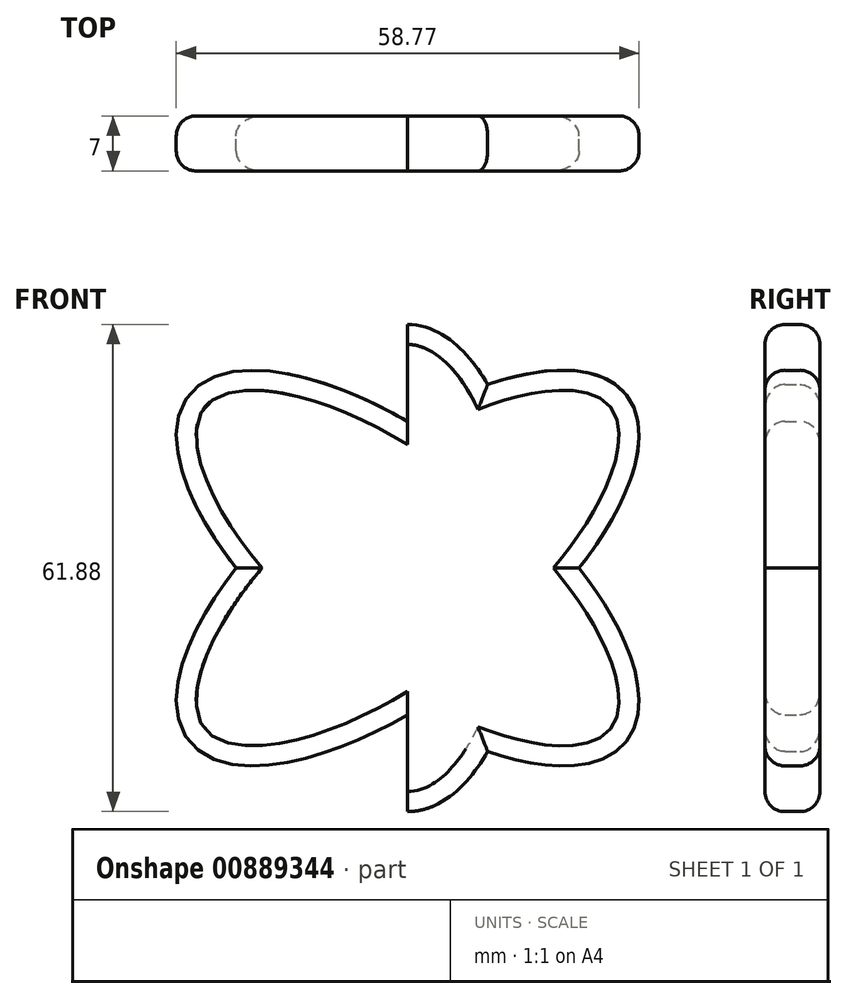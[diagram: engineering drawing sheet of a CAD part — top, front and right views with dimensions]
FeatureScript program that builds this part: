
annotation { "Feature Type Name" : "Feature", "Feature Type Description" : "" }
export const myFeature = defineFeature(function(context is Context, id is Id, definition is map)
    precondition{}
    {
        {
            var Q0;
            Q0=qCreatedBy(makeId("Front.planeOp"),FACE);
            var sketch = newSketch(context, id + "F0", { "sketchPlane" : qUnion([Q0])});
            skEllipse(sketch, "E0", {"center": v(0, 0) * mm, "majorRadius": 30.94 * mm, "minorRadius": 15.45 * mm, "majorAxis": v(0, -1)});
            skEllipse(sketch, "E1", {"center": v(0, 0) * mm, "majorRadius": 35.44 * mm, "minorRadius": 15.45 * mm, "majorAxis": v(0.78, -0.62)});
            skEllipse(sketch, "E2.MirrorC", {"center": v(0, 0) * mm, "majorRadius": 35.44 * mm, "minorRadius": 15.45 * mm, "majorAxis": v(-0.78, -0.62)});
            skLineSegment(sketch, "E3", {"start": v(0, 30.94) * mm, "end": v(0, -30.94) * mm});
            skSolve(sketch);
        }
        {
            var Q0;
            {var subQ0=sQuery(id+"F0.wireOp",EDGE,"E2.MirrorC");var subQ1=sQuery(id+"F0.wireOp",EDGE,"E0");var subQ2=makeQuery(id+"F0.imprint","INTERSECT",VERTEX,{"disambiguationData":[OD(0.0)],"derivedFrom":[subQ1,subQ0]});Q0=makeQuery(id+"F0.imprint","IMPRINT",FACE,{"disambiguationData":[TD([[makeQuery(id+"F0.imprint","IMPRINT",EDGE,{"disambiguationData":[TD([[subQ2,-1.0]])],"derivedFrom":subQ1}),1.0]])]});}
            var Q1;
            {var subQ0=sQuery(id+"F0.wireOp",EDGE,"E1");var subQ1=sQuery(id+"F0.wireOp",EDGE,"E0");var subQ2=makeQuery(id+"F0.imprint","INTERSECT",VERTEX,{"disambiguationData":[OD(1.0)],"derivedFrom":[subQ1,subQ0]});Q1=makeQuery(id+"F0.imprint","IMPRINT",FACE,{"disambiguationData":[TD([[makeQuery(id+"F0.imprint","IMPRINT",EDGE,{"disambiguationData":[TD([[subQ2,-1.0]])],"derivedFrom":subQ1}),-1.0]])]});}
            var Q2;
            {var subQ0=sQuery(id+"F0.wireOp",EDGE,"E2.MirrorC");var subQ1=sQuery(id+"F0.wireOp",EDGE,"E0");var subQ2=makeQuery(id+"F0.imprint","INTERSECT",VERTEX,{"disambiguationData":[OD(0.0)],"derivedFrom":[subQ1,subQ0]});Q2=makeQuery(id+"F0.imprint","IMPRINT",FACE,{"disambiguationData":[TD([[makeQuery(id+"F0.imprint","IMPRINT",EDGE,{"disambiguationData":[TD([[subQ2,1.0]])],"derivedFrom":subQ1}),-1.0]])]});}
            var Q3;
            {var subQ0=sQuery(id+"F0.wireOp",EDGE,"E1");var subQ1=sQuery(id+"F0.wireOp",EDGE,"E0");var subQ2=makeQuery(id+"F0.imprint","INTERSECT",VERTEX,{"disambiguationData":[OD(0.0)],"derivedFrom":[subQ1,subQ0]});Q3=makeQuery(id+"F0.imprint","IMPRINT",FACE,{"disambiguationData":[TD([[makeQuery(id+"F0.imprint","IMPRINT",EDGE,{"disambiguationData":[TD([[subQ2,-1.0]])],"derivedFrom":subQ1}),-1.0]])]});}
            var Q4;
            {var subQ0=sQuery(id+"F0.wireOp",EDGE,"E2.MirrorC");var subQ1=sQuery(id+"F0.wireOp",EDGE,"E0");var subQ2=makeQuery(id+"F0.imprint","INTERSECT",VERTEX,{"disambiguationData":[OD(1.0)],"derivedFrom":[subQ1,subQ0]});Q4=makeQuery(id+"F0.imprint","IMPRINT",FACE,{"disambiguationData":[TD([[makeQuery(id+"F0.imprint","IMPRINT",EDGE,{"disambiguationData":[TD([[subQ2,1.0]])],"derivedFrom":subQ1}),-1.0]])]});}
            var Q5;
            {var subQ0=sQuery(id+"F0.wireOp",EDGE,"E1");var subQ1=sQuery(id+"F0.wireOp",EDGE,"E0");var subQ2=makeQuery(id+"F0.imprint","INTERSECT",VERTEX,{"disambiguationData":[OD(0.0)],"derivedFrom":[subQ1,subQ0]});Q5=makeQuery(id+"F0.imprint","IMPRINT",FACE,{"disambiguationData":[TD([[makeQuery(id+"F0.imprint","IMPRINT",EDGE,{"disambiguationData":[TD([[subQ2,1.0]])],"derivedFrom":subQ1}),1.0]])]});}
            var Q6;
            Q6=makeQuery(id+"F0.imprint","IMPRINT",FACE,{"disambiguationData":[TD([[makeQuery(id+"F0.imprint","IMPRINT",EDGE,{"derivedFrom":sQuery(id+"F0.wireOp",EDGE,"LZZV73RN-npso-72dP-JXCp-cFYvsp7JB5Xd")}),-1.0]])]});
            var Q7;
            {var subQ0=sQuery(id+"F0.wireOp",EDGE,"Dlmi2PQk-qXYu-TZ0k-GXdR-v94EXzE1gpfV");var subQ1=sQuery(id+"F0.wireOp",EDGE,"E2.MirrorC");var subQ2=makeQuery(id+"F0.imprint","INTERSECT",VERTEX,{"disambiguationData":[OD(2.0)],"derivedFrom":[subQ1,subQ0]});Q7=makeQuery(id+"F0.imprint","IMPRINT",FACE,{"disambiguationData":[TD([[makeQuery(id+"F0.imprint","IMPRINT",EDGE,{"disambiguationData":[TD([[subQ2,-1.0]])],"derivedFrom":subQ1}),1.0]])]});}
            var Q8;
            {var subQ0=sQuery(id+"F0.wireOp",EDGE,"Dlmi2PQk-qXYu-TZ0k-GXdR-v94EXzE1gpfV");var subQ1=sQuery(id+"F0.wireOp",EDGE,"E2.MirrorC");var subQ2=makeQuery(id+"F0.imprint","INTERSECT",VERTEX,{"disambiguationData":[OD(0.0)],"derivedFrom":[subQ1,subQ0]});Q8=makeQuery(id+"F0.imprint","IMPRINT",FACE,{"disambiguationData":[TD([[makeQuery(id+"F0.imprint","IMPRINT",EDGE,{"disambiguationData":[TD([[subQ2,-1.0]])],"derivedFrom":subQ1}),1.0]])]});}
            var Q9;
            {var subQ0=sQuery(id+"F0.wireOp",EDGE,"hAAybYIK-r48V-uU67-k7O7-xJTClFqp8aIw");var subQ1=sQuery(id+"F0.wireOp",EDGE,"E1");var subQ2=makeQuery(id+"F0.imprint","INTERSECT",VERTEX,{"disambiguationData":[OD(1.0)],"derivedFrom":[subQ1,subQ0]});Q9=makeQuery(id+"F0.imprint","IMPRINT",FACE,{"disambiguationData":[TD([[makeQuery(id+"F0.imprint","IMPRINT",EDGE,{"disambiguationData":[TD([[subQ2,-1.0]])],"derivedFrom":subQ1}),1.0]])]});}
            var Q10;
            {var subQ0=sQuery(id+"F0.wireOp",EDGE,"hAAybYIK-r48V-uU67-k7O7-xJTClFqp8aIw");var subQ1=sQuery(id+"F0.wireOp",EDGE,"E1");var subQ2=makeQuery(id+"F0.imprint","INTERSECT",VERTEX,{"disambiguationData":[OD(1.0)],"derivedFrom":[subQ1,subQ0]});Q10=makeQuery(id+"F0.imprint","IMPRINT",FACE,{"disambiguationData":[TD([[makeQuery(id+"F0.imprint","IMPRINT",EDGE,{"disambiguationData":[TD([[subQ2,-1.0]])],"derivedFrom":subQ1}),-1.0]])]});}
            var Q11;
            {var subQ0=sQuery(id+"F0.wireOp",EDGE,"E1");var subQ1=sQuery(id+"F0.wireOp",EDGE,"E0");var subQ2=makeQuery(id+"F0.imprint","INTERSECT",VERTEX,{"disambiguationData":[OD(2.0)],"derivedFrom":[subQ1,subQ0]});Q11=makeQuery(id+"F0.imprint","IMPRINT",FACE,{"disambiguationData":[TD([[makeQuery(id+"F0.imprint","IMPRINT",EDGE,{"disambiguationData":[TD([[subQ2,-1.0]])],"derivedFrom":subQ1}),1.0]])]});}
            var Q12;
            {var subQ0=sQuery(id+"F0.wireOp",EDGE,"E2.MirrorC");var subQ1=sQuery(id+"F0.wireOp",EDGE,"E0");var subQ2=makeQuery(id+"F0.imprint","INTERSECT",VERTEX,{"disambiguationData":[OD(0.0)],"derivedFrom":[subQ1,subQ0]});Q12=makeQuery(id+"F0.imprint","IMPRINT",FACE,{"disambiguationData":[TD([[makeQuery(id+"F0.imprint","IMPRINT",EDGE,{"disambiguationData":[TD([[subQ2,1.0]])],"derivedFrom":subQ1}),1.0]])]});}
            var Q13;
            {var subQ0=sQuery(id+"F0.wireOp",EDGE,"hAAybYIK-r48V-uU67-k7O7-xJTClFqp8aIw");var subQ1=sQuery(id+"F0.wireOp",EDGE,"E0");var subQ2=makeQuery(id+"F0.imprint","INTERSECT",VERTEX,{"disambiguationData":[OD(0.0)],"derivedFrom":[subQ1,subQ0]});Q13=makeQuery(id+"F0.imprint","IMPRINT",FACE,{"disambiguationData":[TD([[makeQuery(id+"F0.imprint","IMPRINT",EDGE,{"disambiguationData":[TD([[subQ2,-1.0]])],"derivedFrom":subQ1}),1.0]])]});}
            var Q14;
            {var subQ0=sQuery(id+"F0.wireOp",EDGE,"Dlmi2PQk-qXYu-TZ0k-GXdR-v94EXzE1gpfV");var subQ1=sQuery(id+"F0.wireOp",EDGE,"E0");var subQ2=makeQuery(id+"F0.imprint","INTERSECT",VERTEX,{"disambiguationData":[OD(1.0)],"derivedFrom":[subQ1,subQ0]});Q14=makeQuery(id+"F0.imprint","IMPRINT",FACE,{"disambiguationData":[TD([[makeQuery(id+"F0.imprint","IMPRINT",EDGE,{"disambiguationData":[TD([[subQ2,-1.0]])],"derivedFrom":subQ1}),1.0]])]});}
            var Q15;
            {var subQ0=sQuery(id+"F0.wireOp",EDGE,"Dlmi2PQk-qXYu-TZ0k-GXdR-v94EXzE1gpfV");var subQ1=sQuery(id+"F0.wireOp",EDGE,"E0");var subQ2=makeQuery(id+"F0.imprint","INTERSECT",VERTEX,{"disambiguationData":[OD(1.0)],"derivedFrom":[subQ1,subQ0]});Q15=makeQuery(id+"F0.imprint","IMPRINT",FACE,{"disambiguationData":[TD([[makeQuery(id+"F0.imprint","IMPRINT",EDGE,{"disambiguationData":[TD([[subQ2,-1.0]])],"derivedFrom":subQ1}),-1.0]])]});}
            var Q16;
            {var subQ0=sQuery(id+"F0.wireOp",EDGE,"E2.MirrorC");var subQ1=sQuery(id+"F0.wireOp",EDGE,"E0");var subQ2=makeQuery(id+"F0.imprint","INTERSECT",VERTEX,{"disambiguationData":[OD(2.0)],"derivedFrom":[subQ1,subQ0]});Q16=makeQuery(id+"F0.imprint","IMPRINT",FACE,{"disambiguationData":[TD([[makeQuery(id+"F0.imprint","IMPRINT",EDGE,{"disambiguationData":[TD([[subQ2,-1.0]])],"derivedFrom":subQ1}),-1.0]])]});}
            var Q17;
            {var subQ0=sQuery(id+"F0.wireOp",EDGE,"E2.MirrorC");var subQ1=sQuery(id+"F0.wireOp",EDGE,"E1");var subQ2=makeQuery(id+"F0.imprint","INTERSECT",VERTEX,{"disambiguationData":[OD(0.0)],"derivedFrom":[subQ1,subQ0]});Q17=makeQuery(id+"F0.imprint","IMPRINT",FACE,{"disambiguationData":[TD([[makeQuery(id+"F0.imprint","IMPRINT",EDGE,{"disambiguationData":[TD([[subQ2,-1.0]])],"derivedFrom":subQ1}),1.0]])]});}
            var Q18;
            {var subQ0=sQuery(id+"F0.wireOp",EDGE,"Dlmi2PQk-qXYu-TZ0k-GXdR-v94EXzE1gpfV");var subQ1=sQuery(id+"F0.wireOp",EDGE,"E0");var subQ2=makeQuery(id+"F0.imprint","INTERSECT",VERTEX,{"disambiguationData":[OD(2.0)],"derivedFrom":[subQ1,subQ0]});Q18=makeQuery(id+"F0.imprint","IMPRINT",FACE,{"disambiguationData":[TD([[makeQuery(id+"F0.imprint","IMPRINT",EDGE,{"disambiguationData":[TD([[subQ2,-1.0]])],"derivedFrom":subQ1}),1.0]])]});}
            var Q19;
            {var subQ0=sQuery(id+"F0.wireOp",EDGE,"E1");var subQ1=sQuery(id+"F0.wireOp",EDGE,"E0");var subQ2=makeQuery(id+"F0.imprint","INTERSECT",VERTEX,{"disambiguationData":[OD(1.0)],"derivedFrom":[subQ1,subQ0]});Q19=makeQuery(id+"F0.imprint","IMPRINT",FACE,{"disambiguationData":[TD([[makeQuery(id+"F0.imprint","IMPRINT",EDGE,{"disambiguationData":[TD([[subQ2,-1.0]])],"derivedFrom":subQ1}),1.0]])]});}
            var Q20;
            {var subQ0=sQuery(id+"F0.wireOp",EDGE,"E2.MirrorC");var subQ1=sQuery(id+"F0.wireOp",EDGE,"E1");var subQ2=makeQuery(id+"F0.imprint","INTERSECT",VERTEX,{"disambiguationData":[OD(2.0)],"derivedFrom":[subQ1,subQ0]});Q20=makeQuery(id+"F0.imprint","IMPRINT",FACE,{"disambiguationData":[TD([[makeQuery(id+"F0.imprint","IMPRINT",EDGE,{"disambiguationData":[TD([[subQ2,-1.0]])],"derivedFrom":subQ1}),1.0]])]});}
            var Q21;
            {var subQ0=sQuery(id+"F0.wireOp",EDGE,"E2.MirrorC");var subQ1=sQuery(id+"F0.wireOp",EDGE,"E0");var subQ2=makeQuery(id+"F0.imprint","INTERSECT",VERTEX,{"disambiguationData":[OD(3.0)],"derivedFrom":[subQ1,subQ0]});Q21=makeQuery(id+"F0.imprint","IMPRINT",FACE,{"disambiguationData":[TD([[makeQuery(id+"F0.imprint","IMPRINT",EDGE,{"disambiguationData":[TD([[subQ2,-1.0]])],"derivedFrom":subQ1}),-1.0]])]});}
            var Q22;
            {var subQ0=sQuery(id+"F0.wireOp",EDGE,"E2.MirrorC");var subQ1=sQuery(id+"F0.wireOp",EDGE,"E0");var subQ2=makeQuery(id+"F0.imprint","INTERSECT",VERTEX,{"disambiguationData":[OD(3.0)],"derivedFrom":[subQ1,subQ0]});Q22=makeQuery(id+"F0.imprint","IMPRINT",FACE,{"disambiguationData":[TD([[makeQuery(id+"F0.imprint","IMPRINT",EDGE,{"disambiguationData":[TD([[subQ2,-1.0]])],"derivedFrom":subQ1}),1.0]])]});}
            var Q23;
            {var subQ0=sQuery(id+"F0.wireOp",EDGE,"Dlmi2PQk-qXYu-TZ0k-GXdR-v94EXzE1gpfV");var subQ1=sQuery(id+"F0.wireOp",EDGE,"E0");var subQ2=makeQuery(id+"F0.imprint","INTERSECT",VERTEX,{"disambiguationData":[OD(3.0)],"derivedFrom":[subQ1,subQ0]});Q23=makeQuery(id+"F0.imprint","IMPRINT",FACE,{"disambiguationData":[TD([[makeQuery(id+"F0.imprint","IMPRINT",EDGE,{"disambiguationData":[TD([[subQ2,-1.0]])],"derivedFrom":subQ1}),-1.0]])]});}
            var Q24;
            {var subQ0=sQuery(id+"F0.wireOp",EDGE,"Dlmi2PQk-qXYu-TZ0k-GXdR-v94EXzE1gpfV");var subQ1=sQuery(id+"F0.wireOp",EDGE,"E0");var subQ2=makeQuery(id+"F0.imprint","INTERSECT",VERTEX,{"disambiguationData":[OD(3.0)],"derivedFrom":[subQ1,subQ0]});Q24=makeQuery(id+"F0.imprint","IMPRINT",FACE,{"disambiguationData":[TD([[makeQuery(id+"F0.imprint","IMPRINT",EDGE,{"disambiguationData":[TD([[subQ2,-1.0]])],"derivedFrom":subQ1}),1.0]])]});}
            var Q25;
            {var subQ0=sQuery(id+"F0.wireOp",EDGE,"E1");var subQ1=sQuery(id+"F0.wireOp",EDGE,"E0");var subQ2=makeQuery(id+"F0.imprint","INTERSECT",VERTEX,{"disambiguationData":[OD(3.0)],"derivedFrom":[subQ1,subQ0]});Q25=makeQuery(id+"F0.imprint","IMPRINT",FACE,{"disambiguationData":[TD([[makeQuery(id+"F0.imprint","IMPRINT",EDGE,{"disambiguationData":[TD([[subQ2,-1.0]])],"derivedFrom":subQ1}),1.0]])]});}
            var Q26;
            {var subQ0=sQuery(id+"F0.wireOp",EDGE,"E2.MirrorC");var subQ1=sQuery(id+"F0.wireOp",EDGE,"E0");var subQ2=makeQuery(id+"F0.imprint","INTERSECT",VERTEX,{"disambiguationData":[OD(1.0)],"derivedFrom":[subQ1,subQ0]});Q26=makeQuery(id+"F0.imprint","IMPRINT",FACE,{"disambiguationData":[TD([[makeQuery(id+"F0.imprint","IMPRINT",EDGE,{"disambiguationData":[TD([[subQ2,1.0]])],"derivedFrom":subQ1}),1.0]])]});}
            var Q27;
            {var subQ0=sQuery(id+"F0.wireOp",EDGE,"hAAybYIK-r48V-uU67-k7O7-xJTClFqp8aIw");var subQ1=sQuery(id+"F0.wireOp",EDGE,"E1");var subQ2=makeQuery(id+"F0.imprint","INTERSECT",VERTEX,{"disambiguationData":[OD(3.0)],"derivedFrom":[subQ1,subQ0]});Q27=makeQuery(id+"F0.imprint","IMPRINT",FACE,{"disambiguationData":[TD([[makeQuery(id+"F0.imprint","IMPRINT",EDGE,{"disambiguationData":[TD([[subQ2,-1.0]])],"derivedFrom":subQ1}),-1.0]])]});}
            var Q28;
            {var subQ0=sQuery(id+"F0.wireOp",EDGE,"E2.MirrorC");var subQ1=sQuery(id+"F0.wireOp",EDGE,"E1");var subQ2=makeQuery(id+"F0.imprint","INTERSECT",VERTEX,{"disambiguationData":[OD(1.0)],"derivedFrom":[subQ1,subQ0]});Q28=makeQuery(id+"F0.imprint","IMPRINT",FACE,{"disambiguationData":[TD([[makeQuery(id+"F0.imprint","IMPRINT",EDGE,{"disambiguationData":[TD([[subQ2,-1.0]])],"derivedFrom":subQ1}),1.0]])]});}
            var Q29;
            {var subQ0=sQuery(id+"F0.wireOp",EDGE,"Dlmi2PQk-qXYu-TZ0k-GXdR-v94EXzE1gpfV");var subQ1=sQuery(id+"F0.wireOp",EDGE,"E0");var subQ2=makeQuery(id+"F0.imprint","INTERSECT",VERTEX,{"disambiguationData":[OD(0.0)],"derivedFrom":[subQ1,subQ0]});Q29=makeQuery(id+"F0.imprint","IMPRINT",FACE,{"disambiguationData":[TD([[makeQuery(id+"F0.imprint","IMPRINT",EDGE,{"disambiguationData":[TD([[subQ2,-1.0]])],"derivedFrom":subQ1}),1.0]])]});}
            var Q30;
            {var subQ0=sQuery(id+"F0.wireOp",EDGE,"E2.MirrorC");var subQ1=sQuery(id+"F0.wireOp",EDGE,"E0");var subQ2=makeQuery(id+"F0.imprint","INTERSECT",VERTEX,{"disambiguationData":[OD(2.0)],"derivedFrom":[subQ1,subQ0]});Q30=makeQuery(id+"F0.imprint","IMPRINT",FACE,{"disambiguationData":[TD([[makeQuery(id+"F0.imprint","IMPRINT",EDGE,{"disambiguationData":[TD([[subQ2,-1.0]])],"derivedFrom":subQ1}),1.0]])]});}
            var Q31;
            {var subQ0=sQuery(id+"F0.wireOp",EDGE,"E1");var subQ1=sQuery(id+"F0.wireOp",EDGE,"E0");var subQ2=makeQuery(id+"F0.imprint","INTERSECT",VERTEX,{"disambiguationData":[OD(0.0)],"derivedFrom":[subQ1,subQ0]});Q31=makeQuery(id+"F0.imprint","IMPRINT",FACE,{"disambiguationData":[TD([[makeQuery(id+"F0.imprint","IMPRINT",EDGE,{"disambiguationData":[TD([[subQ2,-1.0]])],"derivedFrom":subQ1}),1.0]])]});}
            var Q32;
            {var subQ0=sQuery(id+"F0.wireOp",EDGE,"E2.MirrorC");var subQ1=sQuery(id+"F0.wireOp",EDGE,"E1");var subQ2=makeQuery(id+"F0.imprint","INTERSECT",VERTEX,{"disambiguationData":[OD(3.0)],"derivedFrom":[subQ1,subQ0]});Q32=makeQuery(id+"F0.imprint","IMPRINT",FACE,{"disambiguationData":[TD([[makeQuery(id+"F0.imprint","IMPRINT",EDGE,{"disambiguationData":[TD([[subQ2,-1.0]])],"derivedFrom":subQ1}),1.0]])]});}
            var Q33;
            {var subQ0=sQuery(id+"F0.wireOp",EDGE,"hAAybYIK-r48V-uU67-k7O7-xJTClFqp8aIw");var subQ1=sQuery(id+"F0.wireOp",EDGE,"E0");var subQ2=makeQuery(id+"F0.imprint","INTERSECT",VERTEX,{"disambiguationData":[OD(2.0)],"derivedFrom":[subQ1,subQ0]});Q33=makeQuery(id+"F0.imprint","IMPRINT",FACE,{"disambiguationData":[TD([[makeQuery(id+"F0.imprint","IMPRINT",EDGE,{"disambiguationData":[TD([[subQ2,-1.0]])],"derivedFrom":subQ1}),1.0]])]});}
            var Q34;
            {var subQ0=sQuery(id+"F0.wireOp",EDGE,"rtznIF7v-u61m-MHR9-NeHj-gsrXDnTg4Oiu");var subQ1=sQuery(id+"F0.wireOp",EDGE,"E1");var subQ2=makeQuery(id+"F0.imprint","INTERSECT",VERTEX,{"disambiguationData":[OD(2.0)],"derivedFrom":[subQ1,subQ0]});Q34=makeQuery(id+"F0.imprint","IMPRINT",FACE,{"disambiguationData":[TD([[makeQuery(id+"F0.imprint","IMPRINT",EDGE,{"disambiguationData":[TD([[subQ2,-1.0]])],"derivedFrom":subQ1}),1.0]])]});}
            var Q35;
            {var subQ0=sQuery(id+"F0.wireOp",EDGE,"hAAybYIK-r48V-uU67-k7O7-xJTClFqp8aIw");var subQ1=sQuery(id+"F0.wireOp",EDGE,"E1");var subQ2=makeQuery(id+"F0.imprint","INTERSECT",VERTEX,{"disambiguationData":[OD(3.0)],"derivedFrom":[subQ1,subQ0]});Q35=makeQuery(id+"F0.imprint","IMPRINT",FACE,{"disambiguationData":[TD([[makeQuery(id+"F0.imprint","IMPRINT",EDGE,{"disambiguationData":[TD([[subQ2,-1.0]])],"derivedFrom":subQ1}),1.0]])]});}
            extrude(context, id + "F1", {"entities" : qUnion([Q0, Q1, Q2, Q3, Q4, Q5, Q6, Q7, Q8, Q9, Q10, Q11, Q12, Q13, Q14, Q15, Q16, Q17, Q18, Q19, Q20, Q21, Q22, Q23, Q24, Q25, Q26, Q27, Q28, Q29, Q30, Q31, Q32, Q33, Q34, Q35]), "depth" : 7 * mm, "offsetDistance" : 25.4 * mm});
        }
        {
            var Q0;
            {var subQ0=sQuery(id+"F0.wireOp",EDGE,"E0");Q0=makeQuery(id+"F1.opExtrude","CAP_EDGE",EDGE,{"disambiguationData":[OSD([subQ0]),TDD([makeQuery(id+"F0.imprint","IMPRINT",EDGE,{"disambiguationData":[TD([[makeQuery(id+"F0.imprint","INTERSECT",VERTEX,{"disambiguationData":[OD(0.0)],"derivedFrom":[subQ0,sQuery(id+"F0.wireOp",EDGE,"E1")]}),1.0]])],"derivedFrom":subQ0})])],"isStart":true});}
            fillet(context, id + "F2", {"entities" : qUnion([Q0]), "radius" : 2.54 * mm, "tangentPropagation" : true, "allowEdgeOverflow" : false});
        }
        {
            var Q0;
            {var subQ0=sQuery(id+"F0.wireOp",EDGE,"E0");Q0=makeQuery(id+"F1.opExtrude","CAP_EDGE",EDGE,{"disambiguationData":[OSD([subQ0]),TDD([makeQuery(id+"F0.imprint","IMPRINT",EDGE,{"disambiguationData":[TD([[makeQuery(id+"F0.imprint","INTERSECT",VERTEX,{"disambiguationData":[OD(0.0)],"derivedFrom":[subQ0,sQuery(id+"F0.wireOp",EDGE,"E2.MirrorC")]}),-1.0]])],"derivedFrom":subQ0})])],"isStart":true});}
            var Q1;
            {var subQ0=sQuery(id+"F0.wireOp",EDGE,"E1");Q1=makeQuery(id+"F1.opExtrude","CAP_EDGE",EDGE,{"disambiguationData":[OSD([subQ0]),TDD([makeQuery(id+"F0.imprint","IMPRINT",EDGE,{"disambiguationData":[TD([[makeQuery(id+"F0.imprint","INTERSECT",VERTEX,{"disambiguationData":[OD(1.0)],"derivedFrom":[sQuery(id+"F0.wireOp",EDGE,"E0"),subQ0]}),-1.0]])],"derivedFrom":subQ0})])],"isStart":true});}
            var Q2;
            {var subQ0=sQuery(id+"F0.wireOp",EDGE,"E2.MirrorC");Q2=makeQuery(id+"F1.opExtrude","CAP_EDGE",EDGE,{"disambiguationData":[OSD([subQ0]),TDD([makeQuery(id+"F0.imprint","IMPRINT",EDGE,{"disambiguationData":[TD([[makeQuery(id+"F0.imprint","INTERSECT",VERTEX,{"disambiguationData":[OD(0.0)],"derivedFrom":[sQuery(id+"F0.wireOp",EDGE,"E0"),subQ0]}),1.0]])],"derivedFrom":subQ0})])],"isStart":true});}
            var Q3;
            {var subQ0=sQuery(id+"F0.wireOp",EDGE,"E1");Q3=makeQuery(id+"F1.opExtrude","CAP_EDGE",EDGE,{"disambiguationData":[OSD([subQ0]),TDD([makeQuery(id+"F0.imprint","IMPRINT",EDGE,{"disambiguationData":[TD([[makeQuery(id+"F0.imprint","INTERSECT",VERTEX,{"disambiguationData":[OD(0.0)],"derivedFrom":[sQuery(id+"F0.wireOp",EDGE,"E0"),subQ0]}),-1.0]])],"derivedFrom":subQ0})])],"isStart":true});}
            var Q4;
            {var subQ0=sQuery(id+"F0.wireOp",EDGE,"E2.MirrorC");Q4=makeQuery(id+"F1.opExtrude","CAP_EDGE",EDGE,{"disambiguationData":[OSD([subQ0]),TDD([makeQuery(id+"F0.imprint","IMPRINT",EDGE,{"disambiguationData":[TD([[makeQuery(id+"F0.imprint","INTERSECT",VERTEX,{"disambiguationData":[OD(1.0)],"derivedFrom":[sQuery(id+"F0.wireOp",EDGE,"E0"),subQ0]}),1.0]])],"derivedFrom":subQ0})])],"isStart":true});}
            fillet(context, id + "F3", {"entities" : qUnion([Q0, Q1, Q2, Q3, Q4]), "radius" : 2.54 * mm, "tangentPropagation" : true, "allowEdgeOverflow" : false});
        }
        {
            var Q0;
            {var subQ0=sQuery(id+"F0.wireOp",EDGE,"E0");Q0=makeQuery(id+"F1.opExtrude","CAP_EDGE",EDGE,{"disambiguationData":[OSD([subQ0]),TDD([makeQuery(id+"F0.imprint","IMPRINT",EDGE,{"disambiguationData":[TD([[makeQuery(id+"F0.imprint","INTERSECT",VERTEX,{"disambiguationData":[OD(0.0)],"derivedFrom":[subQ0,sQuery(id+"F0.wireOp",EDGE,"E2.MirrorC")]}),-1.0]])],"derivedFrom":subQ0})])],"isStart":false});}
            var Q1;
            {var subQ0=sQuery(id+"F0.wireOp",EDGE,"E1");Q1=makeQuery(id+"F1.opExtrude","CAP_EDGE",EDGE,{"disambiguationData":[OSD([subQ0]),TDD([makeQuery(id+"F0.imprint","IMPRINT",EDGE,{"disambiguationData":[TD([[makeQuery(id+"F0.imprint","INTERSECT",VERTEX,{"disambiguationData":[OD(1.0)],"derivedFrom":[sQuery(id+"F0.wireOp",EDGE,"E0"),subQ0]}),-1.0]])],"derivedFrom":subQ0})])],"isStart":false});}
            var Q2;
            {var subQ0=sQuery(id+"F0.wireOp",EDGE,"E2.MirrorC");Q2=makeQuery(id+"F1.opExtrude","CAP_EDGE",EDGE,{"disambiguationData":[OSD([subQ0]),TDD([makeQuery(id+"F0.imprint","IMPRINT",EDGE,{"disambiguationData":[TD([[makeQuery(id+"F0.imprint","INTERSECT",VERTEX,{"disambiguationData":[OD(1.0)],"derivedFrom":[sQuery(id+"F0.wireOp",EDGE,"E0"),subQ0]}),1.0]])],"derivedFrom":subQ0})])],"isStart":false});}
            var Q3;
            {var subQ0=sQuery(id+"F0.wireOp",EDGE,"E1");Q3=makeQuery(id+"F1.opExtrude","CAP_EDGE",EDGE,{"disambiguationData":[OSD([subQ0]),TDD([makeQuery(id+"F0.imprint","IMPRINT",EDGE,{"disambiguationData":[TD([[makeQuery(id+"F0.imprint","INTERSECT",VERTEX,{"disambiguationData":[OD(0.0)],"derivedFrom":[sQuery(id+"F0.wireOp",EDGE,"E0"),subQ0]}),-1.0]])],"derivedFrom":subQ0})])],"isStart":false});}
            var Q4;
            {var subQ0=sQuery(id+"F0.wireOp",EDGE,"E2.MirrorC");Q4=makeQuery(id+"F1.opExtrude","CAP_EDGE",EDGE,{"disambiguationData":[OSD([subQ0]),TDD([makeQuery(id+"F0.imprint","IMPRINT",EDGE,{"disambiguationData":[TD([[makeQuery(id+"F0.imprint","INTERSECT",VERTEX,{"disambiguationData":[OD(0.0)],"derivedFrom":[sQuery(id+"F0.wireOp",EDGE,"E0"),subQ0]}),1.0]])],"derivedFrom":subQ0})])],"isStart":false});}
            fillet(context, id + "F4", {"entities" : qUnion([Q0, Q1, Q2, Q3, Q4]), "radius" : 2.54 * mm, "tangentPropagation" : true, "allowEdgeOverflow" : false});
        }
        {
            var Q0;
            {var subQ0=sQuery(id+"F0.wireOp",EDGE,"E0");Q0=makeQuery(id+"F1.opExtrude","CAP_EDGE",EDGE,{"disambiguationData":[OSD([subQ0]),TDD([makeQuery(id+"F0.imprint","IMPRINT",EDGE,{"disambiguationData":[TD([[makeQuery(id+"F0.imprint","INTERSECT",VERTEX,{"disambiguationData":[OD(0.0)],"derivedFrom":[subQ0,sQuery(id+"F0.wireOp",EDGE,"E1")]}),1.0]])],"derivedFrom":subQ0})])],"isStart":false});}
            fillet(context, id + "F5", {"entities" : qUnion([Q0]), "radius" : 2.54 * mm, "tangentPropagation" : true, "allowEdgeOverflow" : false});
        }
    });
